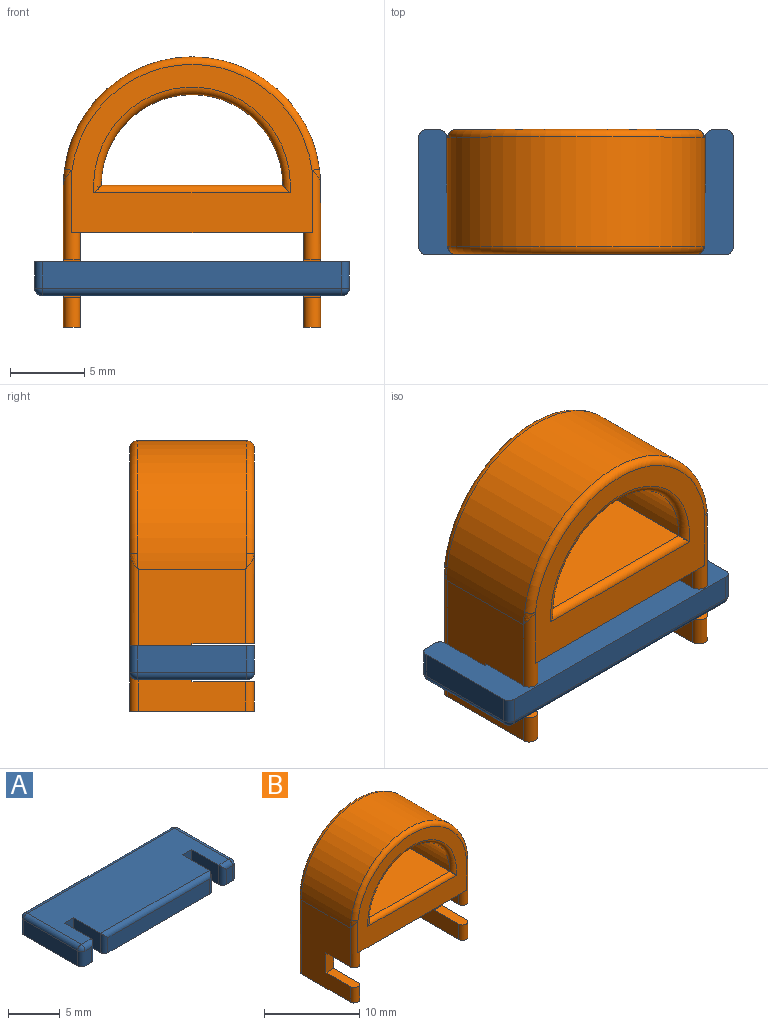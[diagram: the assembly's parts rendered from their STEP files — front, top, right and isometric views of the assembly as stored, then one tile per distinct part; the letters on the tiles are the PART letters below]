
ASSEMBLY  parts=2 mates=1
PART A: 32 faces, bbox 21.1x8.4x2.3 mm
  f0: plane 20.12x1.78mm, normal (0,1,0), area 35.8mm2, adj f13,f19,f25,f28
  f1: plane 7.37x1.78mm, normal (-1,0,0), area 13.1mm2, adj f13,f22,f26,f28
  f2: plane 1.78x0.85mm, normal (0,-1,0), area 1.5mm2, adj f13,f18,f21,f22
  f3: plane 3.68x2.29mm, normal (1,0,0), area 8.4mm2, adj f4,f12,f13,f18
  f4: plane 2.29x1.27mm, normal (0,-1,0), area 2.9mm2, adj f3,f5,f12,f13
  f5: plane 3.68x2.29mm, normal (-1,0,0), area 8.4mm2, adj f4,f12,f13,f31
  f6: plane 13.84x1.78mm, normal (0,-1,0), area 24.6mm2, adj f13,f29,f30,f31
  f7: plane 3.68x2.29mm, normal (1,0,0), area 8.4mm2, adj f8,f12,f13,f29
  f8: plane 2.29x1.27mm, normal (0,-1,0), area 2.9mm2, adj f7,f9,f12,f13
  f9: plane 3.68x2.29mm, normal (-1,0,0), area 8.4mm2, adj f8,f12,f13,f14
  f10: plane 1.78x0.85mm, normal (0,-1,0), area 1.5mm2, adj f13,f14,f15,f16
  f11: plane 7.37x1.78mm, normal (1,0,0), area 13.1mm2, adj f13,f15,f19,f20
  f12: plane 20.12x7.37mm, normal (0,0,1), area 138.8mm2, adj f3,f4,f5,f7,f8,f9,f16,f20
  f13: plane 21.13x8.38mm, normal (0,0,-1), area 166mm2, adj f0,f1,f2,f3,f4,f5,f6,f7
  f14: cylinder r=0.51mm len=2.29mm, axis (0,0,1), area 1.7mm2, adj f9,f10,f13,f16
  f15: cylinder r=0.51mm len=1.78mm, axis (0,0,1), area 1.4mm2, adj f10,f11,f13,f17
  f16: cylinder r=0.51mm len=1.36mm, axis (-1,0,0), area 0.9mm2, adj f10,f12,f14,f17
  f17: sphere r=0.51mm, area 0.4mm2, adj f15,f16,f20
  f18: cylinder r=0.51mm len=2.29mm, axis (0,0,-1), area 1.7mm2, adj f2,f3,f13,f21
  f19: cylinder r=0.51mm len=1.78mm, axis (0,0,-1), area 1.4mm2, adj f0,f11,f13,f23
  f20: cylinder r=0.51mm len=7.37mm, axis (0,-1,0), area 5.9mm2, adj f11,f12,f17,f23
  f21: cylinder r=0.51mm len=1.36mm, axis (-1,0,0), area 0.9mm2, adj f2,f12,f18,f24
  f22: cylinder r=0.51mm len=1.78mm, axis (0,0,-1), area 1.4mm2, adj f1,f2,f13,f24
  f23: sphere r=0.51mm, area 0.4mm2, adj f19,f20,f25
  f24: sphere r=0.51mm, area 0.4mm2, adj f21,f22,f26
  f25: cylinder r=0.51mm len=20.12mm, axis (1,0,0), area 16.1mm2, adj f0,f12,f23,f27
  f26: cylinder r=0.51mm len=7.37mm, axis (0,1,0), area 5.9mm2, adj f1,f12,f24,f27
  f27: sphere r=0.51mm, area 0.4mm2, adj f25,f26,f28
  f28: cylinder r=0.51mm len=1.78mm, axis (0,0,1), area 1.4mm2, adj f0,f1,f13,f27
  f29: cylinder r=0.51mm len=2.29mm, axis (0,0,-1), area 1.7mm2, adj f6,f7,f13,f30
  f30: cylinder r=0.51mm len=14.86mm, axis (-1,0,0), area 11.6mm2, adj f6,f12,f29,f31
  f31: cylinder r=0.51mm len=2.29mm, axis (0,0,1), area 1.7mm2, adj f5,f6,f13,f30
PART B: 34 faces, bbox 18.5x8.6x18.9 mm
  f0: plane 16.13x11.3mm, normal (0,1,0), area 79.7mm2, adj f5,f6,f10,f16,f18,f19
  f1: plane 16.13x11.3mm, normal (0,-1,0), area 79.7mm2, adj f8,f9,f10,f13,f20,f21
  f2: cylinder r=8.64mm len=17.27mm, axis (0,-1,0), area 199.7mm2, adj f4,f7,f12,f13,f14,f15,f16,f17
  f3: plane 12.19x7.37mm, normal (0,0,1), area 89.8mm2, adj f11,f18,f20
  f4: plane 9.53x7.24mm, normal (1,0,0), area 59.8mm2, adj f2,f5,f9,f29,f30,f31,f32,f33
  f5: cylinder r=0.57mm len=10.54mm, axis (0,0,-1), area 14.7mm2, adj f0,f4,f10,f17,f28,f30
  f6: cylinder r=0.57mm len=10.54mm, axis (0,0,-1), area 14.7mm2, adj f0,f7,f10,f15,f23,f24
  f7: plane 9.53x7.24mm, normal (-1,0,0), area 59.8mm2, adj f2,f6,f8,f22,f24,f25,f26,f27
  f8: cylinder r=0.57mm len=6.02mm, axis (0,0,-1), area 6.6mm2, adj f1,f7,f10,f12,f23,f25
  f9: cylinder r=0.57mm len=6.02mm, axis (0,0,-1), area 6.6mm2, adj f1,f4,f10,f14,f28,f32
  f10: plane 16.13x8.38mm, normal (0,0,-1), area 125.9mm2, adj f0,f1,f5,f6,f8,f9,f23,f28
  f11: cylinder r=6.1mm len=12.19mm, axis (0,-1,0), area 141.1mm2, adj f3,f19,f21
  f12: bspline ~1.18x0.67mm, area 0.4mm2, adj f2,f8,f13
  f13: torus R=8.13mm, axis (0,1,0), area 19.5mm2, adj f1,f2,f12,f14
  f14: bspline ~1.18x0.67mm, area 0.4mm2, adj f2,f9,f13
  f15: bspline ~1.18x0.67mm, area 0.4mm2, adj f2,f6,f16
  f16: torus R=8.13mm, axis (0,1,0), area 19.5mm2, adj f0,f2,f15,f17
  f17: bspline ~1.18x0.67mm, area 0.4mm2, adj f2,f5,f16
  f18: cylinder r=0.51mm len=13.17mm, axis (1,0,0), area 10.1mm2, adj f0,f3,f19
  f19: torus R=6.6mm, axis (0,1,0), area 16.1mm2, adj f0,f11,f18
  f20: cylinder r=0.51mm len=13.17mm, axis (-1,0,0), area 10.1mm2, adj f1,f3,f21
  f21: torus R=6.6mm, axis (0,1,0), area 16.1mm2, adj f1,f11,f20
  f22: cylinder r=0.57mm len=1.98mm, axis (0,0,1), area 3.6mm2, adj f7,f23,f24,f26
  f23: plane 7.24x6.35mm, normal (1,0,0), area 36.8mm2, adj f6,f8,f10,f22,f24,f25,f26,f27
  f24: plane 8.38x1.14mm, normal (0,0,-1), area 9.3mm2, adj f6,f7,f22,f23
  f25: plane 4.19x1.14mm, normal (0,0,-1), area 4.7mm2, adj f7,f8,f23,f27
  f26: plane 4.19x1.14mm, normal (0,0,1), area 4.7mm2, adj f7,f22,f23,f27
  f27: plane 2.54x1.14mm, normal (0,-1,0), area 2.9mm2, adj f7,f23,f25,f26
  f28: plane 7.24x6.35mm, normal (-1,0,0), area 36.8mm2, adj f5,f9,f10,f29,f30,f31,f32,f33
  f29: cylinder r=0.57mm len=1.98mm, axis (0,0,1), area 3.6mm2, adj f4,f28,f30,f31
  f30: plane 8.38x1.14mm, normal (0,0,-1), area 9.3mm2, adj f4,f5,f28,f29
  f31: plane 4.19x1.14mm, normal (0,0,1), area 4.7mm2, adj f4,f28,f29,f33
  f32: plane 4.19x1.14mm, normal (0,0,-1), area 4.7mm2, adj f4,f9,f28,f33
  f33: plane 2.54x1.14mm, normal (0,-1,0), area 2.9mm2, adj f4,f28,f31,f32
PLACE A rot(axis=(1,0,0),180deg) t=(-5.19,6.47,2.67)mm
PLACE B t=(-0.76,4.87,4.63)mm
MATE fastened A.f8 <-> B.f33  axis (0,1,0) through (14.15,8.49,1.53)mm
